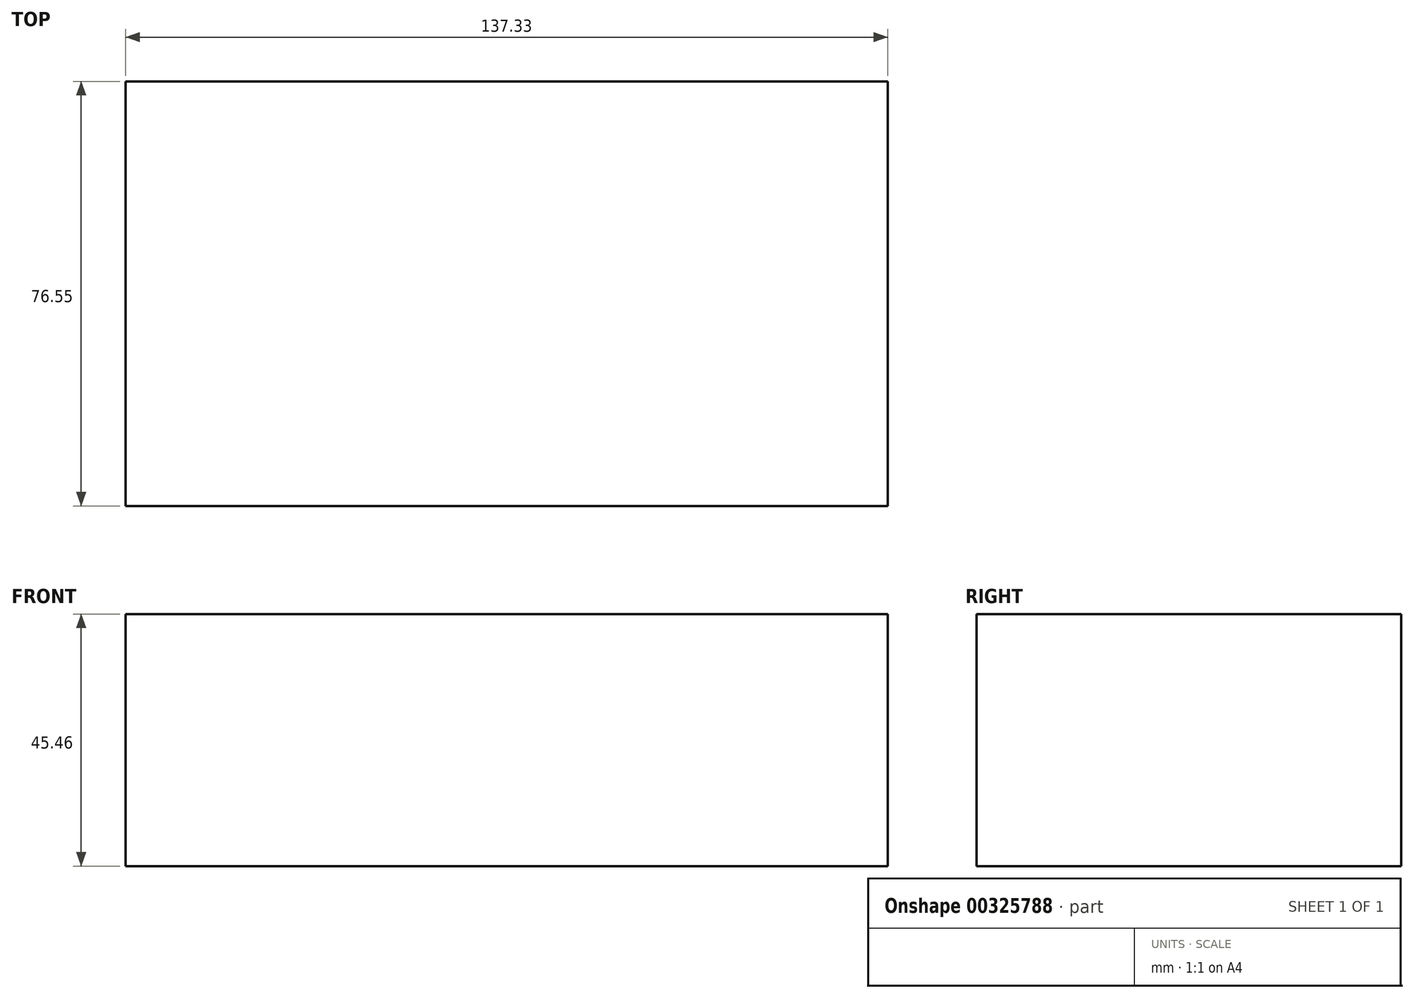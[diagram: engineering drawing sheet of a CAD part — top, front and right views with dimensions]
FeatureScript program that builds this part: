
annotation { "Feature Type Name" : "Feature", "Feature Type Description" : "" }
export const myFeature = defineFeature(function(context is Context, id is Id, definition is map)
    precondition{}
    {
        {
            var Q0;
            Q0=qCreatedBy(makeId("Top.planeOp"),FACE);
            var sketch = newSketch(context, id + "F0", { "sketchPlane" : qUnion([Q0])});
            skLineSegment(sketch, "E0.bottom", {"start": v(69.91, -37.34) * mm, "end": v(-67.42, -37.34) * mm});
            skLineSegment(sketch, "E0.top", {"start": v(69.91, 39.2) * mm, "end": v(-67.42, 39.2) * mm});
            skLineSegment(sketch, "E0.left", {"start": v(69.91, -37.34) * mm, "end": v(69.91, 39.2) * mm});
            skLineSegment(sketch, "E0.right", {"start": v(-67.42, -37.34) * mm, "end": v(-67.42, 39.2) * mm});
            skSolve(sketch);
        }
        {
            var Q0;
            Q0 = qSketchRegion(id + "F0", true);
            var sketch = newSketch(context, id + "F1", { "sketchPlane" : qUnion([Q0])});
            skSolve(sketch);
        }
        {
            var Q0;
            Q0=makeQuery(id+"F0.imprint","IMPRINT",FACE,{"disambiguationData":[TD([[makeQuery(id+"F0.imprint","IMPRINT",EDGE,{"derivedFrom":sQuery(id+"F0.wireOp",EDGE,"E0.bottom")}),-1.0]])]});
            var Q1;
            Q1 = qSketchRegion(id + "F1", true);
            extrude(context, id + "F2", {"entities" : qUnion([Q0, Q1]), "depth" : 45.46 * mm});
        }
    });
